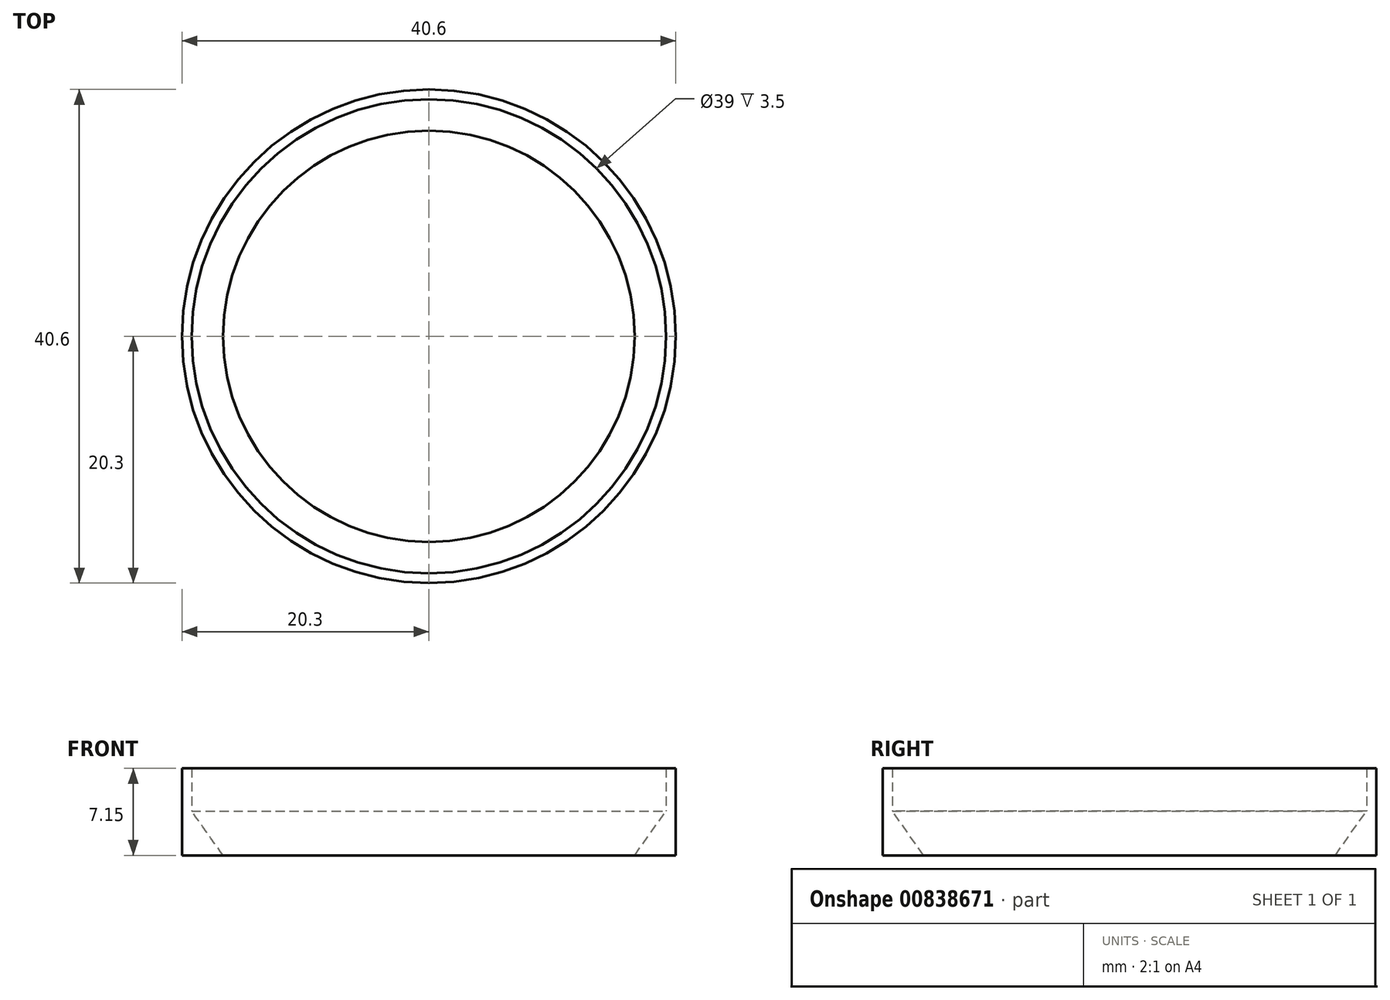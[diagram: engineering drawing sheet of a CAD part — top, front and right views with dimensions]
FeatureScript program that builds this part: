
annotation { "Feature Type Name" : "Feature", "Feature Type Description" : "" }
export const myFeature = defineFeature(function(context is Context, id is Id, definition is map)
    precondition{}
    {
        {
            var Q0;
            Q0=qCreatedBy(makeId("Front.planeOp"),FACE);
            var sketch = newSketch(context, id + "F0", { "sketchPlane" : qUnion([Q0])});
            skLineSegment(sketch, "E0", {"start": v(20.3, 0) * mm, "end": v(20.3, 7.15) * mm});
            skLineSegment(sketch, "E1", {"start": v(20.3, 7.15) * mm, "end": v(19.5, 7.15) * mm});
            skLineSegment(sketch, "E2", {"start": v(19.5, 7.15) * mm, "end": v(19.5, 3.65) * mm});
            skLineSegment(sketch, "E3", {"start": v(19.5, 3.65) * mm, "end": v(16.92, 0) * mm});
            skLineSegment(sketch, "E4", {"start": v(0, 0) * mm, "end": v(0, 5.12) * mm, "construction": true});
            skLineSegment(sketch, "E5", {"start": v(16.92, 0) * mm, "end": v(20.3, 0) * mm});
            skLineSegment(sketch, "E6", {"start": v(0, 5.12) * mm, "end": v(19.5, 5.12) * mm, "construction": true});
            skSolve(sketch);
        }
        {
            var Q0;
            Q0 = qSketchRegion(id + "F0", true);
            var Q1;
            Q1=sQuery(id+"F0.wireOp",EDGE,"E4");
            revolve(context, id + "F1", {"surfaceOperationType" : NewSurfaceOperationType.NEW, "entities" : qUnion([Q0]), "axis" : qUnion([Q1]), "revolveType" : RevolveType.FULL});
        }
    });
